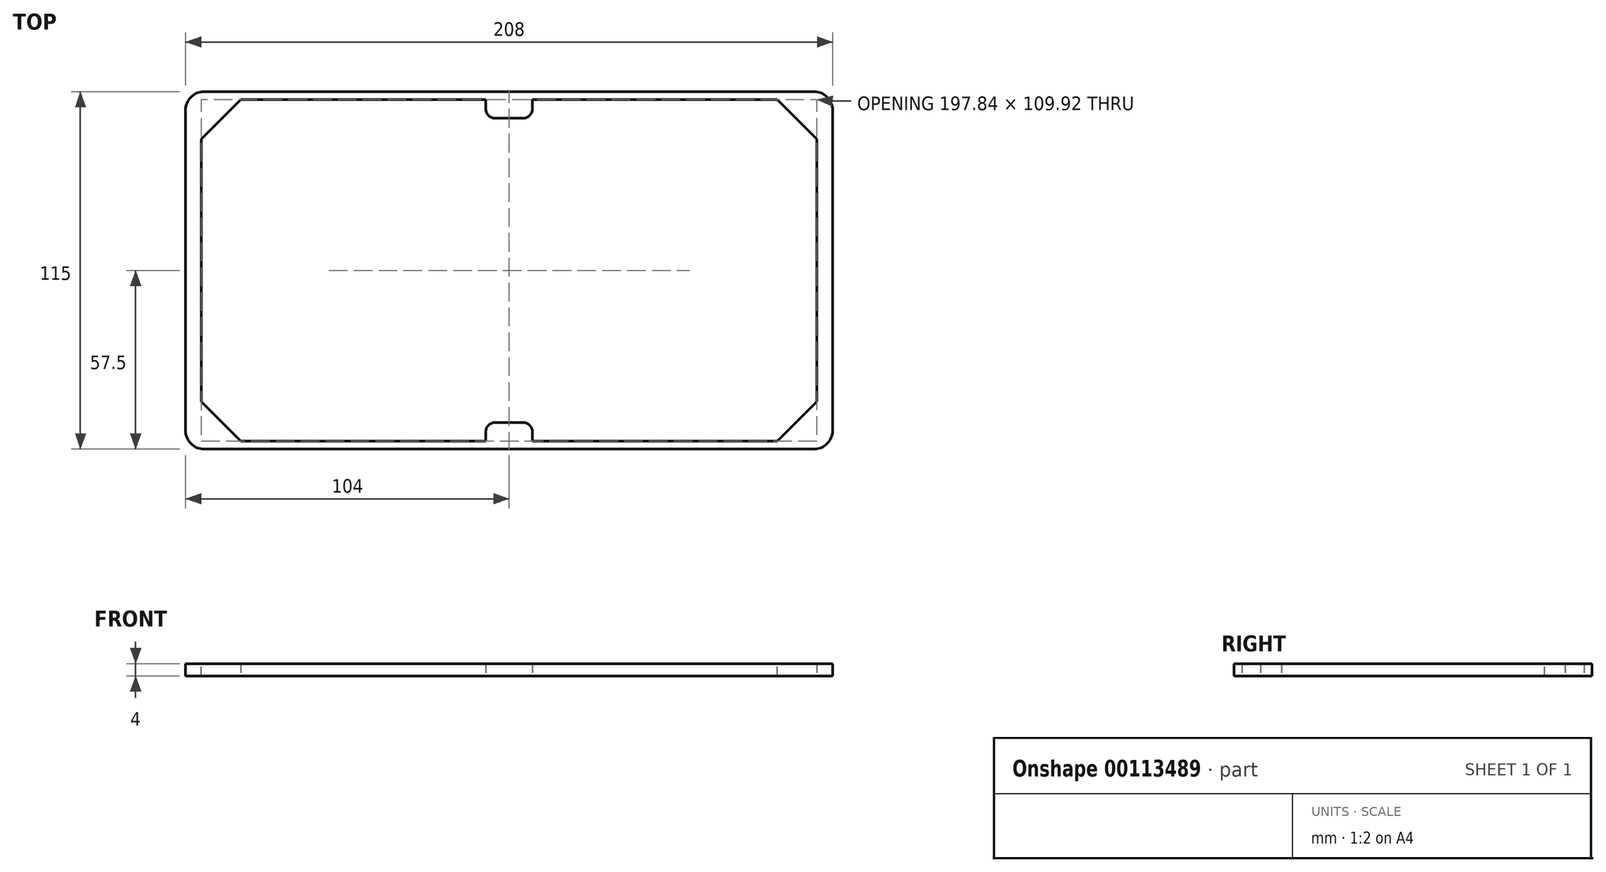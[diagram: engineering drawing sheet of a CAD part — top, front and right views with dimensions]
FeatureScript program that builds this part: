
annotation { "Feature Type Name" : "Feature", "Feature Type Description" : "" }
export const myFeature = defineFeature(function(context is Context, id is Id, definition is map)
    precondition{}
    {
        {
            var Q0;
            Q0=qCreatedBy(makeId("Top.planeOp"),FACE);
            var sketch = newSketch(context, id + "F0", { "sketchPlane" : qUnion([Q0])});
            skLineSegment(sketch, "E0.bottom", {"start": v(0, 0) * mm, "end": v(208, 0) * mm});
            skLineSegment(sketch, "E0.top", {"start": v(0, 115) * mm, "end": v(208, 115) * mm});
            skLineSegment(sketch, "E0.left", {"start": v(0, 0) * mm, "end": v(0, 115) * mm});
            skLineSegment(sketch, "E0.right", {"start": v(208, 0) * mm, "end": v(208, 115) * mm});
            skLineSegment(sketch, "E1.bottom", {"start": v(5.08, 112.46) * mm, "end": v(202.92, 112.46) * mm});
            skLineSegment(sketch, "E1.top", {"start": v(5.08, 2.54) * mm, "end": v(202.92, 2.54) * mm});
            skLineSegment(sketch, "E1.left", {"start": v(5.08, 112.46) * mm, "end": v(5.08, 2.54) * mm});
            skLineSegment(sketch, "E1.right", {"start": v(202.92, 112.46) * mm, "end": v(202.92, 2.54) * mm});
            skSolve(sketch);
        }
        {
            var Q0;
            Q0=qSketchRegion(id+"F0",true);
            extrude(context, id + "F1", {"entities" : qUnion([Q0]), "depth" : 4 * mm});
        }
        {
            var Q0;
            Q0=makeQuery(id+"F1.opExtrude","SWEPT_EDGE",EDGE,{"disambiguationData":[OSD([sQuery(id+"F0.wireOp",EDGE,"E0.top"),sQuery(id+"F0.wireOp",EDGE,"E0.left")])]});
            var Q1;
            Q1=makeQuery(id+"F1.opExtrude","SWEPT_EDGE",EDGE,{"disambiguationData":[OSD([sQuery(id+"F0.wireOp",EDGE,"E0.top"),sQuery(id+"F0.wireOp",EDGE,"E0.right")])]});
            var Q2;
            Q2=makeQuery(id+"F1.opExtrude","SWEPT_EDGE",EDGE,{"disambiguationData":[OSD([sQuery(id+"F0.wireOp",EDGE,"E0.bottom"),sQuery(id+"F0.wireOp",EDGE,"E0.right")])]});
            var Q3;
            Q3=makeQuery(id+"F1.opExtrude","SWEPT_EDGE",EDGE,{"disambiguationData":[OSD([sQuery(id+"F0.wireOp",EDGE,"E0.bottom"),sQuery(id+"F0.wireOp",EDGE,"E0.left")])]});
            fillet(context, id + "F2", {"entities" : qUnion([Q0, Q1, Q2, Q3]), "radius" : 6 * mm, "tangentPropagation" : true, "defaultsChanged" : false, "vertexSettings" : [], "allowEdgeOverflow" : false});
        }
        {
            var Q0;
            Q0=makeQuery(id+"F1.opExtrude","SWEPT_EDGE",EDGE,{"disambiguationData":[OSD([sQuery(id+"F0.wireOp",EDGE,"E1.bottom"),sQuery(id+"F0.wireOp",EDGE,"E1.left")])]});
            var Q1;
            Q1=makeQuery(id+"F1.opExtrude","SWEPT_EDGE",EDGE,{"disambiguationData":[OSD([sQuery(id+"F0.wireOp",EDGE,"E1.top"),sQuery(id+"F0.wireOp",EDGE,"E1.right")])]});
            var Q2;
            Q2=makeQuery(id+"F1.opExtrude","SWEPT_EDGE",EDGE,{"disambiguationData":[OSD([sQuery(id+"F0.wireOp",EDGE,"E1.bottom"),sQuery(id+"F0.wireOp",EDGE,"E1.right")])]});
            var Q3;
            Q3=makeQuery(id+"F1.opExtrude","SWEPT_EDGE",EDGE,{"disambiguationData":[OSD([sQuery(id+"F0.wireOp",EDGE,"E1.top"),sQuery(id+"F0.wireOp",EDGE,"E1.left")])]});
            chamfer(context, id + "F3", {"entities" : qUnion([Q0, Q1, Q2, Q3]), "width" : 12.7 * mm, "tangentPropagation" : true});
        }
        {
            var Q0;
            Q0=makeQuery(id+"F1.opExtrude","SWEPT_FACE",FACE,{"disambiguationData":[OSD([sQuery(id+"F0.wireOp",EDGE,"E1.top")])]});
            var sketch = newSketch(context, id + "F4", { "sketchPlane" : qUnion([Q0])});
            skLineSegment(sketch, "E2.bottom", {"start": v(-111.5, 4) * mm, "end": v(-96.5, 4) * mm});
            skLineSegment(sketch, "E2.top", {"start": v(-111.5, 0) * mm, "end": v(-96.5, 0) * mm});
            skLineSegment(sketch, "E2.left", {"start": v(-111.5, 4) * mm, "end": v(-111.5, 0) * mm});
            skLineSegment(sketch, "E2.right", {"start": v(-96.5, 4) * mm, "end": v(-96.5, 0) * mm});
            skSolve(sketch);
        }
        {
            var Q0;
            Q0=qSketchRegion(id+"F4",true);
            extrude(context, id + "F5", {"entities" : qUnion([Q0]), "operationType" : NewBodyOperationType.ADD, "depth" : 6 * mm, "offsetDistance" : 25 * mm});
        }
        {
            var Q0;
            Q0=makeQuery(id+"F1.opExtrude","SWEPT_FACE",FACE,{"disambiguationData":[OSD([sQuery(id+"F0.wireOp",EDGE,"E1.bottom")])]});
            var sketch = newSketch(context, id + "F6", { "sketchPlane" : qUnion([Q0])});
            skLineSegment(sketch, "E3.bottom", {"start": v(96.5, 4) * mm, "end": v(111.5, 4) * mm});
            skLineSegment(sketch, "E3.top", {"start": v(96.5, 0) * mm, "end": v(111.5, 0) * mm});
            skLineSegment(sketch, "E3.left", {"start": v(96.5, 4) * mm, "end": v(96.5, 0) * mm});
            skLineSegment(sketch, "E3.right", {"start": v(111.5, 4) * mm, "end": v(111.5, 0) * mm});
            skSolve(sketch);
        }
        {
            var Q0;
            Q0=qSketchRegion(id+"F6",true);
            extrude(context, id + "F7", {"entities" : qUnion([Q0]), "operationType" : NewBodyOperationType.ADD, "depth" : 6 * mm, "offsetDistance" : 25 * mm});
        }
        {
            var Q0;
            Q0=makeQuery(id+"F7.opExtrude","CAP_EDGE",EDGE,{"disambiguationData":[OSD([sQuery(id+"F6.wireOp",EDGE,"E3.left")])],"isStart":false});
            var Q1;
            Q1=makeQuery(id+"F7.opExtrude","CAP_EDGE",EDGE,{"disambiguationData":[OSD([sQuery(id+"F6.wireOp",EDGE,"E3.right")])],"isStart":false});
            var Q2;
            Q2=makeQuery(id+"F5.opExtrude","CAP_EDGE",EDGE,{"disambiguationData":[OSD([sQuery(id+"F4.wireOp",EDGE,"E2.left")])],"isStart":false});
            var Q3;
            Q3=makeQuery(id+"F5.opExtrude","CAP_EDGE",EDGE,{"disambiguationData":[OSD([sQuery(id+"F4.wireOp",EDGE,"E2.right")])],"isStart":false});
            fillet(context, id + "F8", {"entities" : qUnion([Q0, Q1, Q2, Q3]), "tangentPropagation" : true, "radius" : 3 * mm, "defaultsChanged" : true, "vertexSettings" : [], "allowEdgeOverflow" : false});
        }
    });
